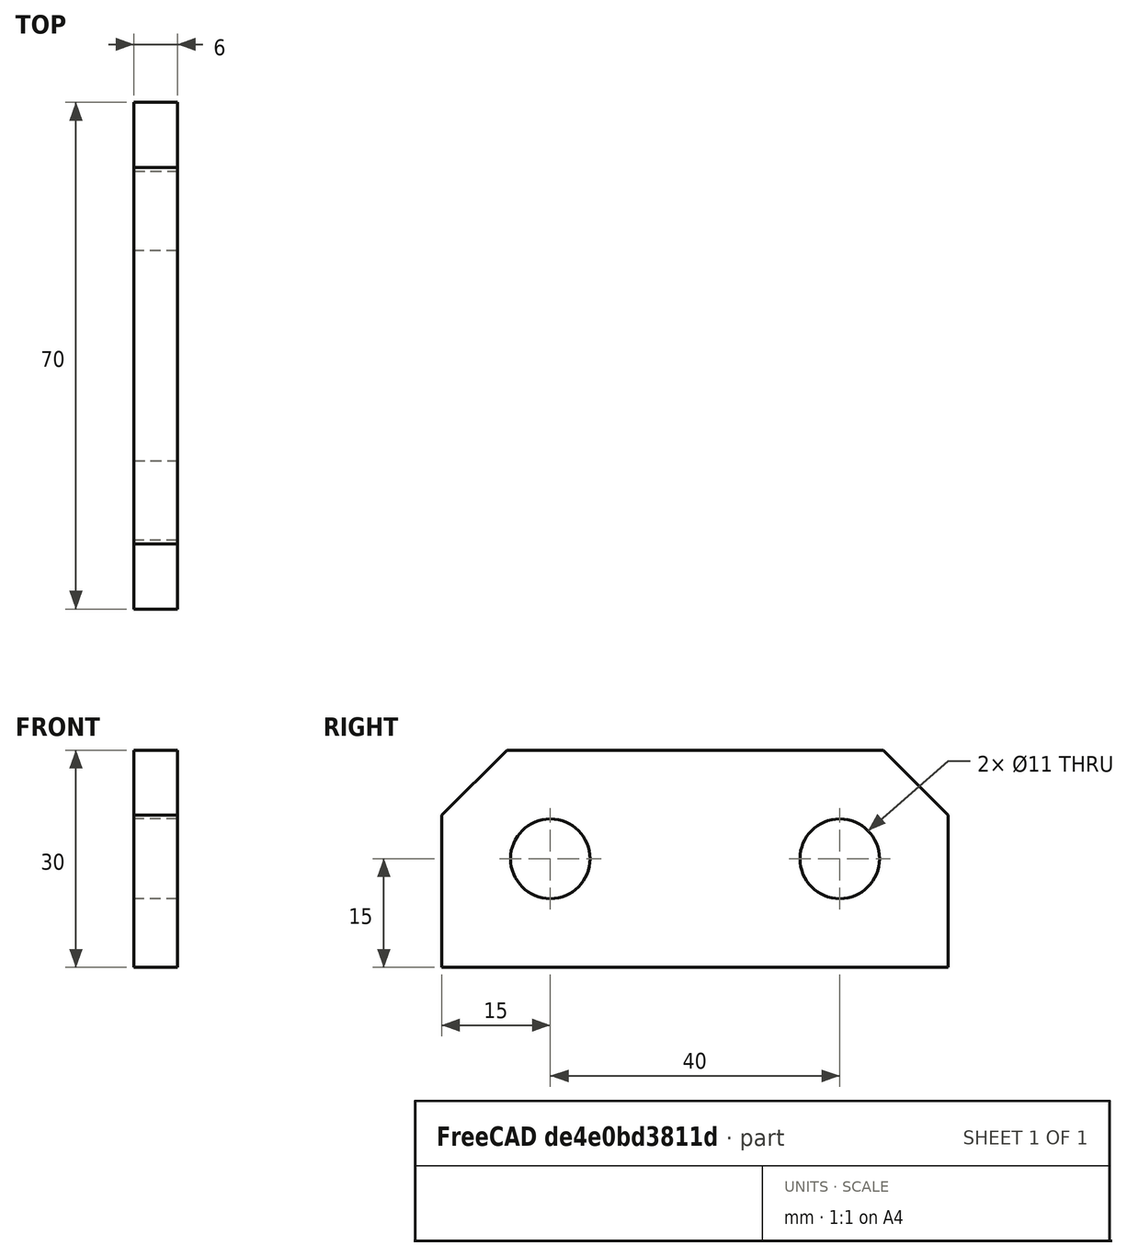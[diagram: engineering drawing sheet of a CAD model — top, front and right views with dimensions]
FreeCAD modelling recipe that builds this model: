
FCSTD DOCUMENT  (FreeCAD 0.21R33668 +26 (Git))
Label: keyplate
License: All rights reserved
LicenseURL: http://en.wikipedia.org/wiki/All_rights_reserved
objects: Sketcher::SketchObject×1, PartDesign::Pad×1, PartDesign::Body×1, Spreadsheet::Sheet×1
note: 4 computed .brp shape members not serialized (recipe doc carries the construction recipe); baked Part::Feature solids carry a one-line shape summary decoded from their .brp

FEATURE [Sketcher::SketchObject] Sketch
  FullyConstrained = true
  MapMode = 5
  Placement = pos=(0,0,0) rot=(0.57735,0.57735,0.57735;2.0944rad)
  Support = -> [YZ_Plane]
  expr: Constraints[12] = Spreadsheet.G2
  expr: Constraints[13] = Spreadsheet.C2
  expr: Constraints[14] = Spreadsheet.D2
  expr: Constraints[15] = Spreadsheet.G2
  expr: Constraints[17] = Spreadsheet.B2 / 2 - Spreadsheet.J6
  expr: Constraints[19] = Spreadsheet.F2
  expr: Constraints[1] = Spreadsheet.B2
  expr: Constraints[21] = Spreadsheet.E2
  expr: Constraints[22] = Spreadsheet.C2 / 2
  sketch-geometry (9):
    g0: Circle CenterX=0 CenterY=0 CenterZ=0 NormalX=0 NormalY=0 NormalZ=1 AngleXU=0 Radius=17.5
    g1: LineSegment StartX=-26 StartY=35.5 StartZ=0 EndX=26 EndY=35.5 EndZ=0
    g2: LineSegment StartX=35 StartY=26.5 StartZ=0 EndX=35 EndY=5.5 EndZ=0
    g3: LineSegment StartX=35 StartY=5.5 StartZ=0 EndX=-35 EndY=5.5 EndZ=0
    g4: LineSegment StartX=-35 StartY=5.5 StartZ=0 EndX=-35 EndY=26.5 EndZ=0
    g5: LineSegment StartX=-35 StartY=26.5 StartZ=0 EndX=-26 EndY=35.5 EndZ=0
    g6: LineSegment StartX=26 StartY=35.5 StartZ=0 EndX=35 EndY=26.5 EndZ=0
    g7: Circle CenterX=-20 CenterY=20.5 CenterZ=0 NormalX=0 NormalY=0 NormalZ=1 AngleXU=0 Radius=5.5
    g8: Circle CenterX=20 CenterY=20.5 CenterZ=0 NormalX=0 NormalY=0 NormalZ=1 AngleXU=0 Radius=5.5
  constraints (23):
    c: Coincident(g0,g-1)
    c: Diameter(g0) = 35
    c: Coincident(g2,g3)
    c: Coincident(g3,g4)
    c: Vertical(g2)
    c: Vertical(g4)
    c: Coincident(g2,g6)
    c: Coincident(g1,g6)
    c: Coincident(g1,g5)
    c: Coincident(g4,g5)
    c: Symmetric(g3,g2,g-2)
    c: Equal(g5,g6)
    c: DistanceY(g4,g1) = 9
    c: DistanceY(g2,g1) = 30
    c: DistanceX(g3,g3) = 70
    c: DistanceX(g4,g1) = 9
    c: Symmetric(g1,g1,g-2)
    c: Distance(g0,g3) = 5.5
    c: Equal(g7,g8)
    c: Diameter(g7) = 11
    c: Symmetric(g7,g8,g-2)
    c: DistanceX(g7,g8) = 40
    c: Distance(g7,g1) = 15
FEATURE [PartDesign::Pad] Pad
  Direction = (1,-2e-16,3e-16)
  Length = 6
  Length2 = 10
  Placement = pos=(0,0,0) rot=(1,1,1;2.0944rad)
  Profile = -> Sketch
  ReferenceAxis = -> Sketch [N_Axis]
  Type = 0
FEATURE [PartDesign::Body] Body
  Group = -> [Sketch,Pad]
  Origin = -> Origin
  Tip = -> Pad
FEATURE [Spreadsheet::Sheet] Spreadsheet
  cells = A1='min; B1='max; C1='a; D1='b; E1='c; F1='d; G1='e; H1='f; I1='g; J1='h; K1='n; B2=35; C2(a0)=30; D2(b0)=70; E2(c0)=40; F2(d0)=11; G2(e0)=9; H2(f0)=6; I2(g0)=12; J2(h0)=6; K2(n0)=1; A3=30; B3=40; C3=30; D3=70; E3=40; F3=11; G3=9; H3=6; I3=12; J3=6; K3=1; A4=40; B4=50; C4=40; D4=90; E4=50; F4=14; G4=12; H4=6; I4=12; J4=8; K4=1; A5=50; B5=60; C5=40; D5=100; E5=60; F5=18; G5=12; H5=8; I5=12; J5=10; K5=1; A6=60; B6=75; C6=40; D6=120; E6=80; F6=18; G6=12; H6=10; I6=15; J6=12; K6=1; A7=75; B7=95; C7=50; D7=150; E7=100; F7=22; G7=15; H7=12; I7=18; J7=14; K7=1; A8=95; B8=120; C8=50; D8=170; E8=120; F8=22; G8=15; H8=12; I8=18; J8=16; K8=2; A9=120; B9=150; C9=60; D9=210; E9=150; F9=24; G9=18; H9=10; I9=24; J9=20; K9=2; A10=150; B10=190; C10=60; D10=250; E10=190; F10=27; G10=18; H10=20; I10=30; J10=25; K10=2
